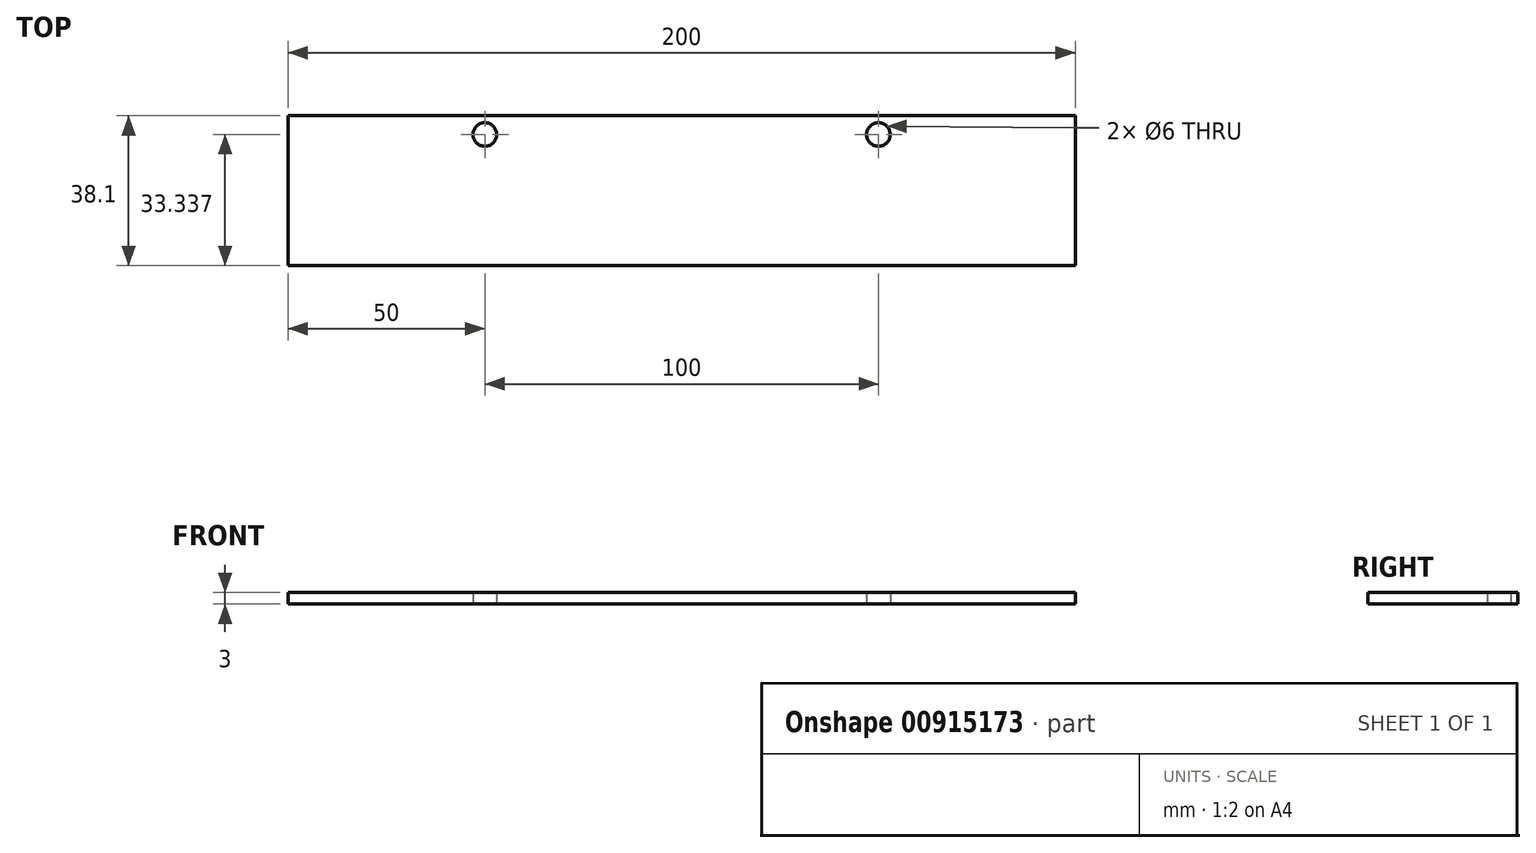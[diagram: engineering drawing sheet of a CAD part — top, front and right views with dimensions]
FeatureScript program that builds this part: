
annotation { "Feature Type Name" : "Feature", "Feature Type Description" : "" }
export const myFeature = defineFeature(function(context is Context, id is Id, definition is map)
    precondition{}
    {
        {
            var Q0;
            Q0=qCreatedBy(makeId("Top.planeOp"),FACE);
            var sketch = newSketch(context, id + "F0", { "sketchPlane" : qUnion([Q0])});
            skLineSegment(sketch, "E0.bottom", {"start": v(-100, 19.05) * mm, "end": v(100, 19.05) * mm});
            skLineSegment(sketch, "E0.top", {"start": v(-100, -19.05) * mm, "end": v(100, -19.05) * mm});
            skLineSegment(sketch, "E0.left", {"start": v(-100, 19.05) * mm, "end": v(-100, -19.05) * mm});
            skLineSegment(sketch, "E0.right", {"start": v(100, 19.05) * mm, "end": v(100, -19.05) * mm});
            skPoint(sketch, "E0.middle", {"position": v(0, 0) * mm});
            skLineSegment(sketch, "E1", {"start": v(0, 0) * mm, "end": v(0, 19.05) * mm});
            skPoint(sketch, "E2", {"position": v(0, 9.52) * mm});
            skLineSegment(sketch, "E3", {"start": v(0, 9.52) * mm, "end": v(0, 19.05) * mm});
            skPoint(sketch, "E4", {"position": v(0, 14.29) * mm});
            skLineSegment(sketch, "E5", {"start": v(0, 14.29) * mm, "end": v(100, 14.29) * mm});
            skPoint(sketch, "E6", {"position": v(50, 14.29) * mm});
            skLineSegment(sketch, "E7", {"start": v(0, 14.29) * mm, "end": v(-100, 14.29) * mm});
            skLineSegment(sketch, "E8", {"start": v(-100, 14.29) * mm, "end": v(-50, 14.29) * mm});
            skCircle(sketch, "E9", {"center": v(-50, 14.29) * mm, "radius": 3 * mm});
            skCircle(sketch, "E10", {"center": v(50, 14.29) * mm, "radius": 3 * mm});
            skLineSegment(sketch, "E11", {"start": v(-50, 14.29) * mm, "end": v(-50, 11.29) * mm});
            skLineSegment(sketch, "E12", {"start": v(50, 14.29) * mm, "end": v(50, 11.29) * mm});
            skSolve(sketch);
        }
        {
            var Q0;
            {var subQ3=sQuery(id+"F0.wireOp",EDGE,"E0.bottom");Q0=makeQuery(id+"F0.imprint","IMPRINT",FACE,{"disambiguationData":[TD([[makeQuery(id+"F0.imprint","IMPRINT",EDGE,{"derivedFrom":subQ3}),-1.0]])]});}
            var Q1;
            {var subQ16=sQuery(id+"F0.wireOp",EDGE,"E0.top");Q1=makeQuery(id+"F0.imprint","IMPRINT",FACE,{"disambiguationData":[TD([[makeQuery(id+"F0.imprint","IMPRINT",EDGE,{"derivedFrom":subQ16}),1.0]])]});}
            extrude(context, id + "F1", {"entities" : qUnion([Q0, Q1]), "depth" : 3 * mm, "offsetDistance" : 25 * mm});
        }
    });
